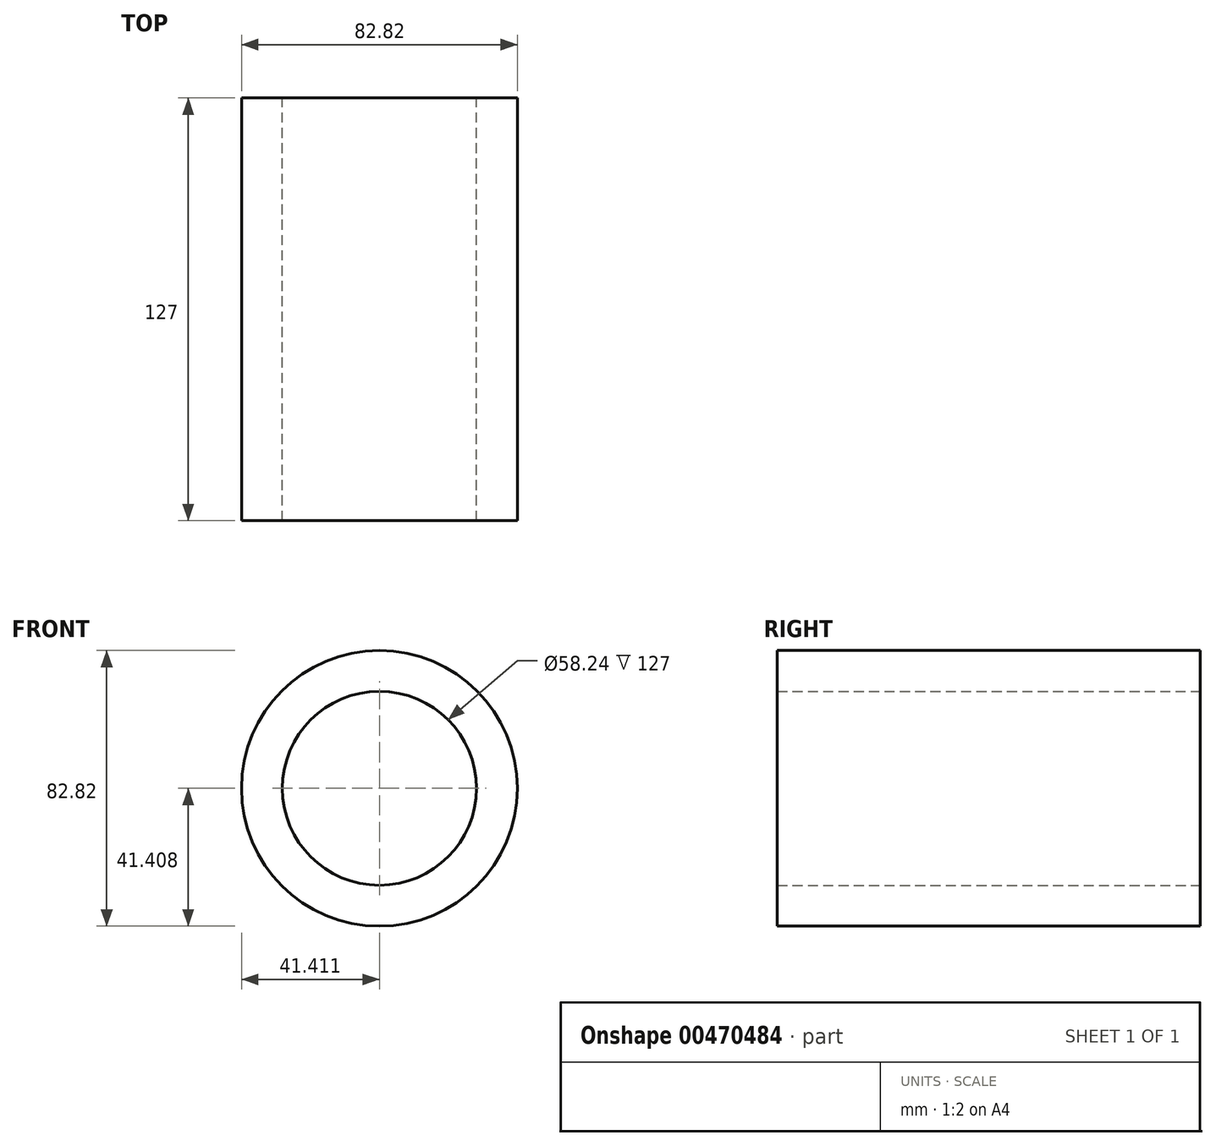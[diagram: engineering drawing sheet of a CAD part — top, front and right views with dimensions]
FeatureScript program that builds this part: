
annotation { "Feature Type Name" : "Feature", "Feature Type Description" : "" }
export const myFeature = defineFeature(function(context is Context, id is Id, definition is map)
    precondition{}
    {
        {
            var Q0;
            Q0=qCreatedBy(makeId("Front.planeOp"),FACE);
            var sketch = newSketch(context, id + "F0", { "sketchPlane" : qUnion([Q0])});
            skCircle(sketch, "E0", {"center": v(-32.63, 25.5) * mm, "radius": 29.12 * mm});
            skCircle(sketch, "E1", {"center": v(-32.63, 25.5) * mm, "radius": 41.41 * mm});
            skSolve(sketch);
        }
        {
            var Q0;
            Q0=makeQuery(id+"F0.imprint","IMPRINT",FACE,{"disambiguationData":[TD([[makeQuery(id+"F0.imprint","IMPRINT",EDGE,{"derivedFrom":sQuery(id+"F0.wireOp",EDGE,"E0")}),-1.0]])]});
            extrude(context, id + "F1", {"entities" : qUnion([Q0]), "depth" : 127 * mm});
        }
    });
